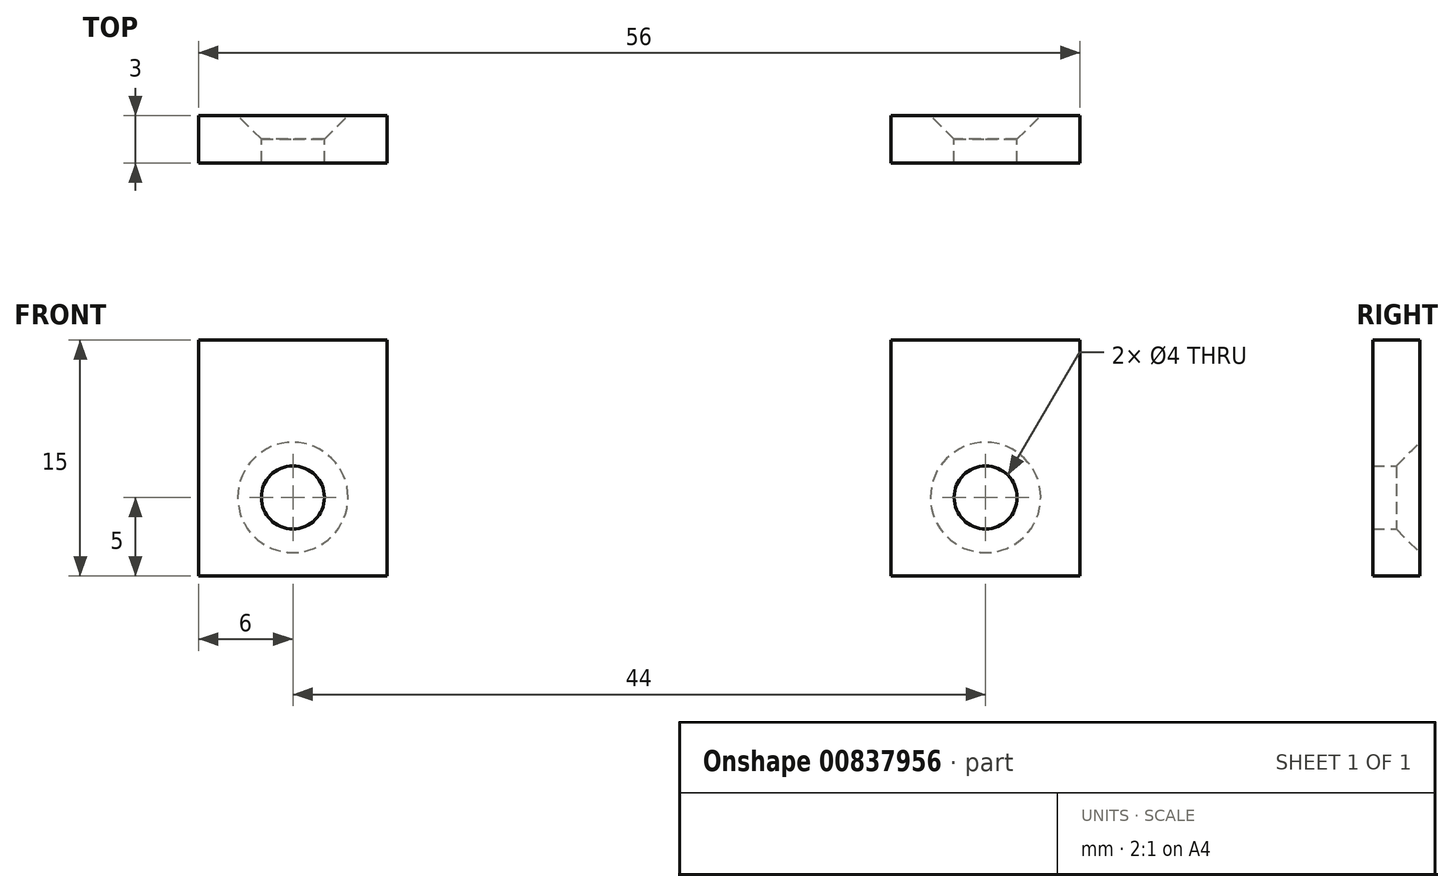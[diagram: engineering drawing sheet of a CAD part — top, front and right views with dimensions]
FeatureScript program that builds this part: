
annotation { "Feature Type Name" : "Feature", "Feature Type Description" : "" }
export const myFeature = defineFeature(function(context is Context, id is Id, definition is map)
    precondition{}
    {
        {
            var Q0;
            Q0=qCreatedBy(makeId("Top.planeOp"),FACE);
            var sketch = newSketch(context, id + "F0", { "sketchPlane" : qUnion([Q0])});
            skLineSegment(sketch, "E0", {"start": v(0, 0) * mm, "end": v(15, 0) * mm});
            skLineSegment(sketch, "E1", {"start": v(15, 0) * mm, "end": v(15, 9) * mm});
            skLineSegment(sketch, "E2", {"start": v(15, 9) * mm, "end": v(41, 9) * mm});
            skLineSegment(sketch, "E3", {"start": v(41, 9) * mm, "end": v(41, 0) * mm});
            skLineSegment(sketch, "E4", {"start": v(41, 0) * mm, "end": v(56, 0) * mm});
            skLineSegment(sketch, "E5.0", {"start": v(44, 3) * mm, "end": v(56, 3) * mm});
            skLineSegment(sketch, "E5.1", {"start": v(0, 3) * mm, "end": v(12, 3) * mm});
            skLineSegment(sketch, "E5.2", {"start": v(12, 3) * mm, "end": v(12, 12) * mm});
            skLineSegment(sketch, "E5.3", {"start": v(12, 12) * mm, "end": v(44, 12) * mm});
            skLineSegment(sketch, "E5.4", {"start": v(44, 12) * mm, "end": v(44, 3) * mm});
            skLineSegment(sketch, "E6", {"start": v(0, 0) * mm, "end": v(0, 3) * mm});
            skLineSegment(sketch, "E7", {"start": v(56, 3) * mm, "end": v(56, 0) * mm});
            skSolve(sketch);
        }
        {
            var Q0;
            Q0 = qSketchRegion(id + "F0", true);
            extrude(context, id + "F1", {"entities" : qUnion([Q0]), "depth" : 15 * mm, "offsetDistance" : 25 * mm});
        }
        {
            var Q0;
            Q0=makeQuery(id+"F1.opExtrude","SWEPT_FACE",FACE,{"disambiguationData":[OSD([sQuery(id+"F0.wireOp",EDGE,"E5.3")])]});
            var sketch = newSketch(context, id + "F2", { "sketchPlane" : qUnion([Q0])});
            skLineSegment(sketch, "E8", {"start": v(-44, 11) * mm, "end": v(-12, 11) * mm, "construction": true});
            skLineSegment(sketch, "E9", {"start": v(-28, 0) * mm, "end": v(-28, 15) * mm, "construction": true});
            skLineSegment(sketch, "E10", {"start": v(-36, 15) * mm, "end": v(-36, 7) * mm, "construction": true});
            skCircle(sketch, "E11", {"center": v(-36, 11) * mm, "radius": 2 * mm});
            skCircle(sketch, "E12.MirrorC", {"center": v(-20, 11) * mm, "radius": 2 * mm});
            skSolve(sketch);
        }
        {
            var Q0;
            Q0=makeQuery(id+"F2.imprint","IMPRINT",FACE,{"disambiguationData":[TD([[makeQuery(id+"F2.imprint","IMPRINT",EDGE,{"derivedFrom":sQuery(id+"F2.wireOp",EDGE,"E11")}),1.0]])]});
            var Q1;
            Q1 = qSketchRegion(id + "F2", true);
            var Q2;
            Q2=makeQuery(id+"F2.imprint","IMPRINT",FACE,{"disambiguationData":[TD([[makeQuery(id+"F2.imprint","IMPRINT",EDGE,{"derivedFrom":sQuery(id+"F2.wireOp",EDGE,"E12.MirrorC")}),-1.0]])]});
            extrude(context, id + "F3", {"entities" : qUnion([Q0, Q1, Q2]), "operationType" : NewBodyOperationType.REMOVE, "oppositeDirection" : true, "depth" : 25 * mm, "offsetDistance" : 25 * mm});
        }
        {
            var Q0;
            Q0=makeQuery(id+"F1.opExtrude","SWEPT_FACE",FACE,{"disambiguationData":[OSD([sQuery(id+"F0.wireOp",EDGE,"E5.1")])]});
            var sketch = newSketch(context, id + "F4", { "sketchPlane" : qUnion([Q0])});
            skLineSegment(sketch, "E13", {"start": v(-6, 0) * mm, "end": v(-6, 15) * mm, "construction": true});
            skLineSegment(sketch, "E14", {"start": v(-12, 5) * mm, "end": v(0, 5) * mm, "construction": true});
            skPoint(sketch, "E15", {"position": v(-6, 5) * mm});
            skLineSegment(sketch, "E16", {"start": v(-28, 0) * mm, "end": v(-28, 15.11) * mm, "construction": true});
            skPoint(sketch, "E17.MirrorP", {"position": v(-50, 5) * mm});
            skSolve(sketch);
        }
        {
            var Q0;
            Q0=sQuery(id+"F4.wireOp",VERTEX,"E15");
            var Q1;
            Q1=sQuery(id+"F4.wireOp",VERTEX,"E17.MirrorP");
            var Q2;
            Q2=makeQuery(id+"F1.opExtrude","SWEPT_BODY",BODY,{"disambiguationData":[OSD([sQuery(id+"F0.wireOp",EDGE,"E0"),sQuery(id+"F0.wireOp",EDGE,"E1"),sQuery(id+"F0.wireOp",EDGE,"E2"),sQuery(id+"F0.wireOp",EDGE,"E3"),sQuery(id+"F0.wireOp",EDGE,"E4"),sQuery(id+"F0.wireOp",EDGE,"E5.0"),sQuery(id+"F0.wireOp",EDGE,"E5.1"),sQuery(id+"F0.wireOp",EDGE,"E5.2"),sQuery(id+"F0.wireOp",EDGE,"E5.3"),sQuery(id+"F0.wireOp",EDGE,"E5.4"),sQuery(id+"F0.wireOp",EDGE,"E6"),sQuery(id+"F0.wireOp",EDGE,"E7")])]});
            hole(context, id + "F5", {"style" : HoleStyle.C_SINK, "endStyle" : HoleEndStyle.THROUGH, "holeDiameter" : 4 * mm, "cSinkDiameter" : 7 * mm, "cSinkAngle" : 90 * degree, "majorDiameter" : 5 * mm, "isTappedThrough" : true, "tappedDepth" : 12 * mm, "tapClearance" : 3, "locations" : qUnion([Q0, Q1]), "scope" : qUnion([Q2])});
        }
    });
